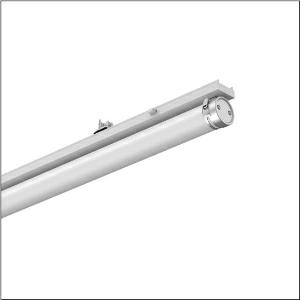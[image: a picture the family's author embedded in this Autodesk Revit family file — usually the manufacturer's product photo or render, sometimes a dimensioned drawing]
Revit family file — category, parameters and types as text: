
# Revit family: monsun_r__31_tube_51ft10nn4a0atr2_f2a8
name_source: partatom
category: Lighting Fixtures
units: mm (PartAtom-declared; Revit-internal decimal feet)

## family parameters
Cut with Voids When Loaded = No
Host = Face
Light Source = No
Part Type = Normal
Room Calculation Point = No
Round Connector Dimension = Use Diameter
Shared = No

## types (1)
- --- (1 x LED, 10000 lm, 58 W, 4000K)
    Apparent Load = 58 VA
    CIE Flux Codes = 42 71 90 91 100
    Color Rendering = 80
    Color Temperature = 4000K
    Default Elevation = 1800 mm
    Description = Monsun® 31 Tube, tubular luminaire, primary optical cover: diffuser, of PMMA, light emission: direct distribution, primary light characteristic: symmetric, LED, rated luminous flux: 10.000lm, luminous efficacy: 172lm/W, light colour: 840, colour temperature: 4000K, with with 1 terminal, 5-pole, max. 2.5mm², mains connection: 220..240V, AC, 50/60Hz, rated input power: 58W, housing, cylindrical, of PMMA, semi-transparent, matt white, with luminaire and ceiling fastening, V4A, mounting with brackets of stainless steel, length: 1.500mm, diameter: 75mm, end cap, of stainless steel (V4A), protection rating (complete): IP20, protection rating (lamp compartment): IP67/69K, insulation class (complete): insulation class I (protective earthing), certification: CE, UKCA, impact resistance: IK06, permissible operating ambient temperature: -20..+40°C, corresponds to IFS (International Featured Standards) requirements for safety and quality in the food industry, contact your sales advisor before using the luminaires in applications with unclear chemical exposure, large temperature fluctuations or condensation-forming humidity, packaging unit: 1 piece
    Height = 132 mm
    Lamp = 1 x LED
    Lamp Light Flux = 10000 lm
    Lamp Power = 58 W
    Lamp count = 1
    Length = 1500 mm
    Luminous efficacy = 172 lm/W
    Manufacturer = Siteco
    ModVariant = No
    Model = 51FT10NN4A0ATR2
    Mounting Place = Ceiling
    Mounting Type = Pendant
    Number of Poles = 1
    OnlyDefault = Yes
    Power Factor = 1
    Product Name = Monsun® 31 Tube
    Product group = tubular luminaire
    ProductGroupID = 906
    Protection Class = Protection class I
    Protection Degree = IP 20
    RLX_Detail_Level = 1
    RLX_Emergency_Light_Flux = 0 lm
    RLX_Emergency_Type = 0
    RLX_Emergency_Type_DB = No
    RlxData = <blob elided: 32337 chars, md5=4e7fbae8>
    Socket = socket
    Standby Power = 0 W
    System Light Flux = 10000 lm
    System Power = 58 W
    Type Comments = individual setting: luminous flux: 100 % | (OFF | OFF | ON | OFF) | 350 mA
    Type Image = l_1242814.jpg
    URL = http://relux.com
    VarID = @adj_074679
    Voltage = 0 V
    Weight = 0.00 kg
    Width = 79 mm

## geometry (parser evidence)
native form markers: Blend x4, Sweep x11
no freeform markers — native parametric forms only
